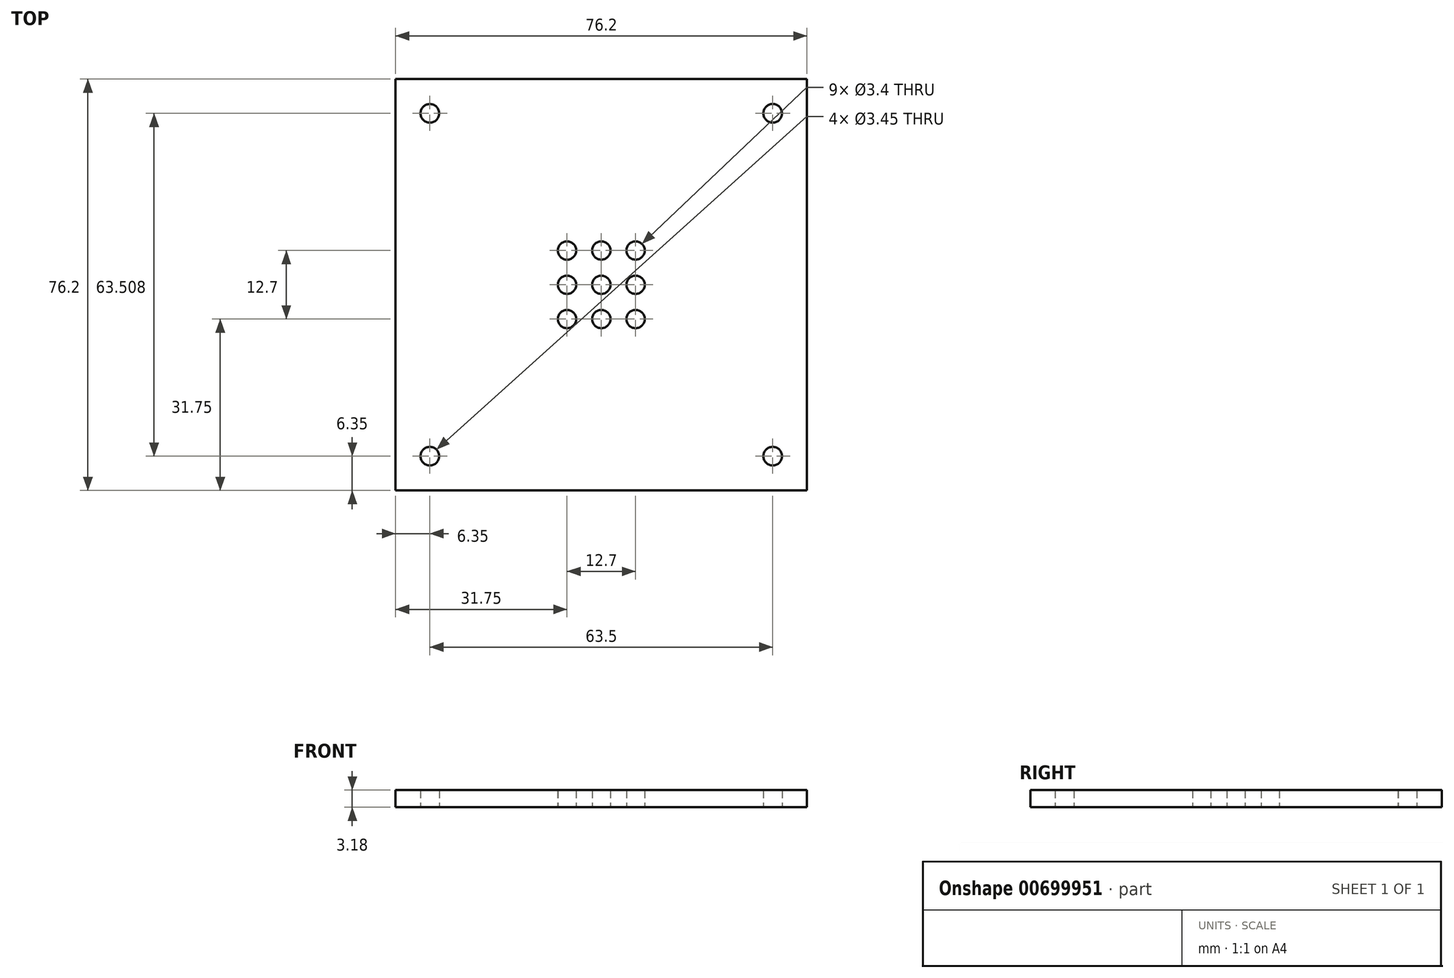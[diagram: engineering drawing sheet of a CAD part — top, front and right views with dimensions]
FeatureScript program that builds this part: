
annotation { "Feature Type Name" : "Feature", "Feature Type Description" : "" }
export const myFeature = defineFeature(function(context is Context, id is Id, definition is map)
    precondition{}
    {
        {
            var Q0;
            Q0=qCreatedBy(makeId("Top.planeOp"),FACE);
            var sketch = newSketch(context, id + "F0", { "sketchPlane" : qUnion([Q0])});
            skLineSegment(sketch, "E0.bottom", {"start": v(38.1, 38.1) * mm, "end": v(-38.1, 38.1) * mm});
            skLineSegment(sketch, "E0.top", {"start": v(38.1, -38.1) * mm, "end": v(-38.1, -38.1) * mm});
            skLineSegment(sketch, "E0.left", {"start": v(38.1, 38.1) * mm, "end": v(38.1, -38.1) * mm});
            skLineSegment(sketch, "E0.right", {"start": v(-38.1, 38.1) * mm, "end": v(-38.1, -38.1) * mm});
            skPoint(sketch, "E0.middle", {"position": v(0, 0) * mm});
            skCircle(sketch, "E1", {"center": v(-31.75, 31.75) * mm, "radius": 1.73 * mm});
            skCircle(sketch, "E2", {"center": v(-31.75, -31.75) * mm, "radius": 1.73 * mm});
            skCircle(sketch, "E3", {"center": v(31.75, -31.75) * mm, "radius": 1.73 * mm});
            skCircle(sketch, "E4", {"center": v(31.75, 31.76) * mm, "radius": 1.73 * mm});
            skCircle(sketch, "E5", {"center": v(0, 0) * mm, "radius": 1.7 * mm});
            skCircle(sketch, "E6.0.1.0", {"center": v(0, 6.35) * mm, "radius": 1.7 * mm});
            skCircle(sketch, "E6.1.0.0", {"center": v(6.35, 0) * mm, "radius": 1.7 * mm});
            skCircle(sketch, "E6.1.1.0", {"center": v(6.35, 6.35) * mm, "radius": 1.7 * mm});
            skLineSegment(sketch, "E6.direction1", {"start": v(0, 0) * mm, "end": v(6.35, 0) * mm, "construction": true});
            skLineSegment(sketch, "E6.direction2", {"start": v(0, 0) * mm, "end": v(0, 6.35) * mm, "construction": true});
            skCircle(sketch, "E7.1.0.0", {"center": v(-6.35, 0) * mm, "radius": 1.7 * mm});
            skLineSegment(sketch, "E7.direction1", {"start": v(0, 0) * mm, "end": v(-6.35, 0) * mm, "construction": true});
            skCircle(sketch, "E8.0.1.0", {"center": v(-6.35, -6.35) * mm, "radius": 1.7 * mm});
            skCircle(sketch, "E8.0.1.1", {"center": v(0, -6.35) * mm, "radius": 1.7 * mm});
            skCircle(sketch, "E8.0.1.2", {"center": v(6.35, -6.35) * mm, "radius": 1.7 * mm});
            skLineSegment(sketch, "E8.direction1", {"start": v(-6.35, 0) * mm, "end": v(19.05, 0) * mm, "construction": true});
            skLineSegment(sketch, "E8.direction2", {"start": v(-6.35, 0) * mm, "end": v(-6.35, -6.35) * mm, "construction": true});
            skCircle(sketch, "E9", {"center": v(-6.35, 6.35) * mm, "radius": 1.7 * mm});
            skSolve(sketch);
        }
        {
            var Q0;
            Q0=makeQuery(id+"F0.imprint","IMPRINT",FACE,{"disambiguationData":[TD([[makeQuery(id+"F0.imprint","IMPRINT",EDGE,{"derivedFrom":sQuery(id+"F0.wireOp",EDGE,"E0.bottom")}),1.0]])]});
            extrude(context, id + "F1", {"entities" : qUnion([Q0]), "depth" : 3.17 * mm, "offsetDistance" : 25.4 * mm});
        }
    });
